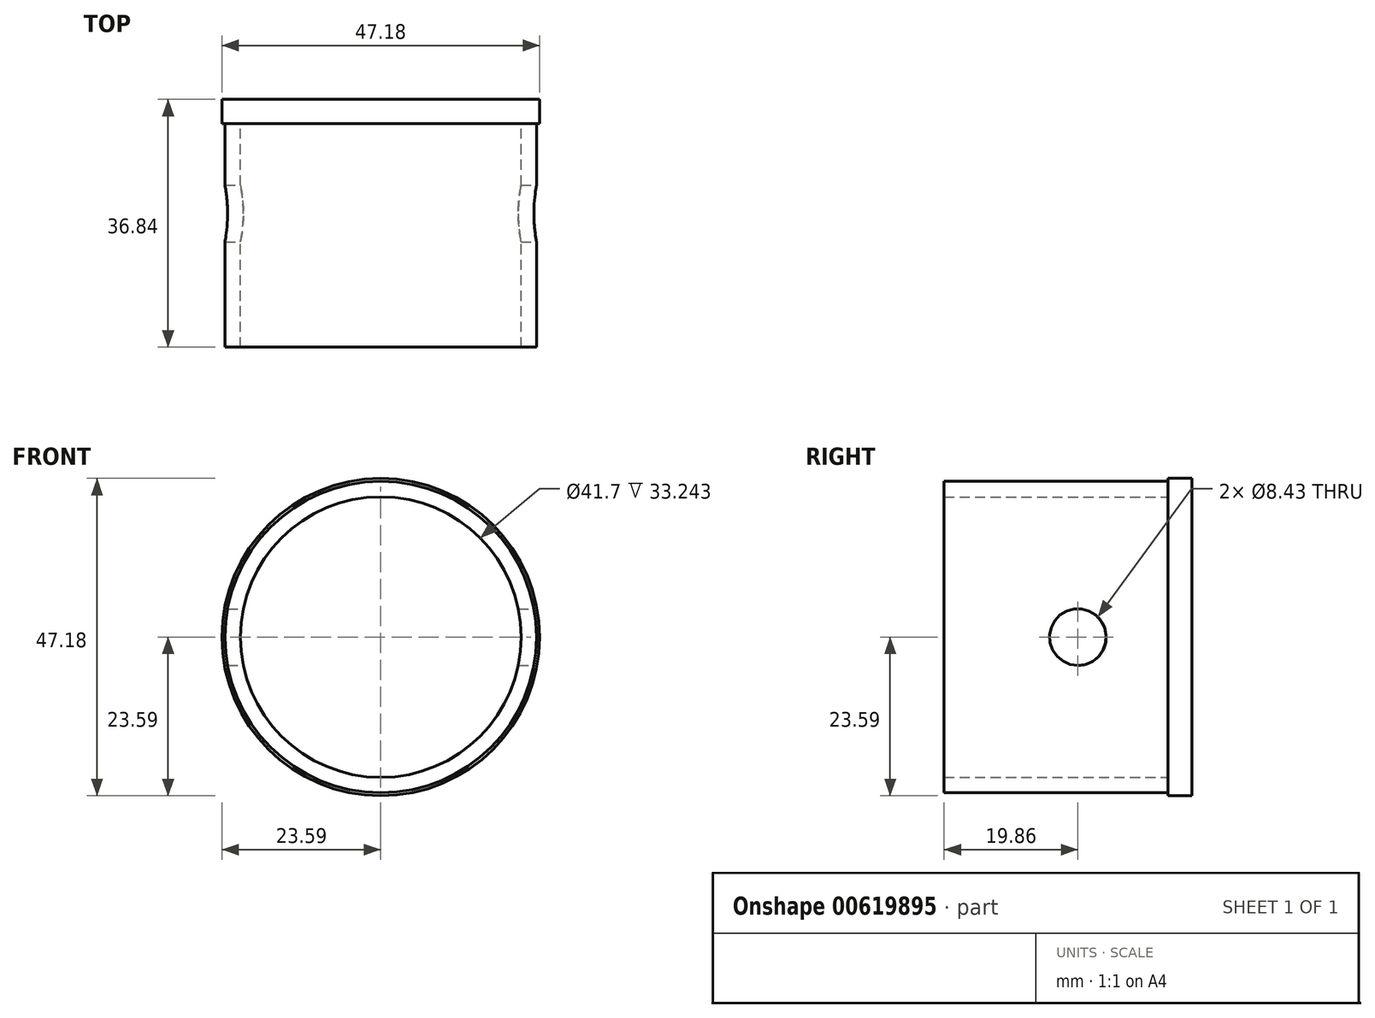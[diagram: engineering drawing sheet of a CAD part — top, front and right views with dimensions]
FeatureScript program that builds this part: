
annotation { "Feature Type Name" : "Feature", "Feature Type Description" : "" }
export const myFeature = defineFeature(function(context is Context, id is Id, definition is map)
    precondition{}
    {
        {
            var Q0;
            Q0=qCreatedBy(makeId("Front.planeOp"),FACE);
            var sketch = newSketch(context, id + "F0", { "sketchPlane" : qUnion([Q0])});
            skCircle(sketch, "E0", {"center": v(0, 0) * mm, "radius": 23.14 * mm});
            skCircle(sketch, "E1", {"center": v(0, 0) * mm, "radius": 20.85 * mm});
            skSolve(sketch);
        }
        {
            var Q0;
            Q0 = qSketchRegion(id + "F0", true);
            extrude(context, id + "F1", {"entities" : qUnion([Q0]), "depth" : 33.24 * mm, "offsetDistance" : 25.4 * mm});
        }
        {
            var Q0;
            Q0=qCreatedBy(makeId("Front.planeOp"),FACE);
            var sketch = newSketch(context, id + "F2", { "sketchPlane" : qUnion([Q0])});
            skCircle(sketch, "E2", {"center": v(0, 0) * mm, "radius": 23.59 * mm});
            skSolve(sketch);
        }
        {
            var Q0;
            Q0 = qSketchRegion(id + "F2", true);
            extrude(context, id + "F3", {"entities" : qUnion([Q0]), "operationType" : NewBodyOperationType.ADD, "oppositeDirection" : true, "depth" : 3.6 * mm, "offsetDistance" : 25.4 * mm});
        }
        {
            var Q0;
            Q0=qCreatedBy(makeId("Right.planeOp"),FACE);
            var sketch = newSketch(context, id + "F4", { "sketchPlane" : qUnion([Q0])});
            skCircle(sketch, "E3", {"center": v(-13.38, 0) * mm, "radius": 4.21 * mm});
            skSolve(sketch);
        }
        {
            var Q0;
            Q0 = qSketchRegion(id + "F4", true);
            extrude(context, id + "F5", {"entities" : qUnion([Q0]), "operationType" : NewBodyOperationType.REMOVE, "endBound" : BoundingType.SYMMETRIC, "oppositeDirection" : true, "depth" : 106.7 * mm, "offsetDistance" : 25.4 * mm});
        }
    });
